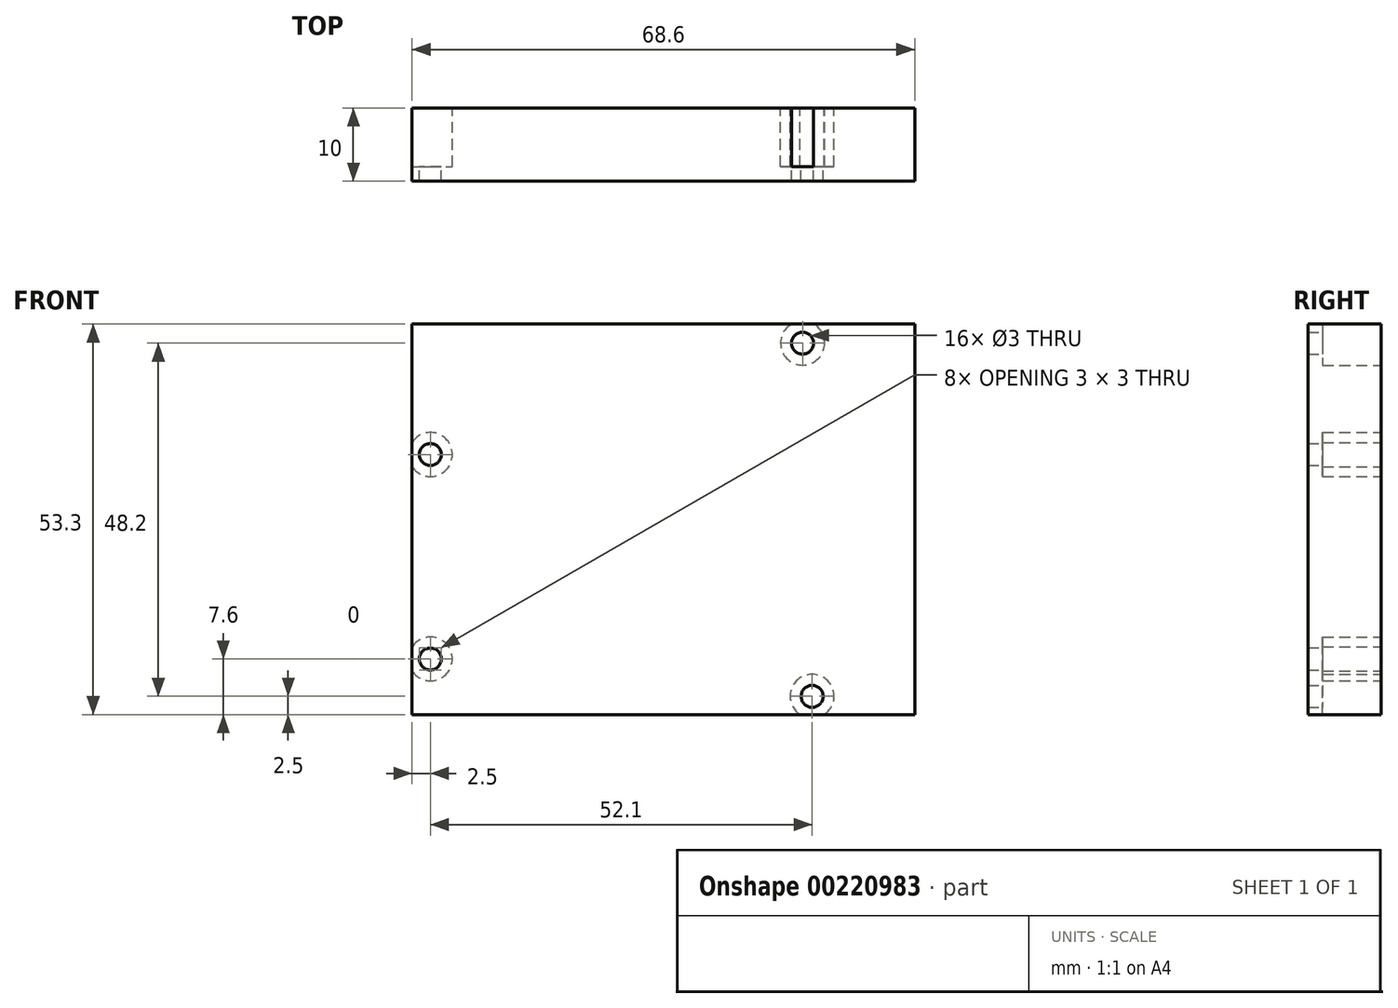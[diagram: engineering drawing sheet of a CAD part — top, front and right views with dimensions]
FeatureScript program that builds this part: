
annotation { "Feature Type Name" : "Feature", "Feature Type Description" : "" }
export const myFeature = defineFeature(function(context is Context, id is Id, definition is map)
    precondition{}
    {
        {
            var Q0;
            Q0=qCreatedBy(makeId("Front.planeOp"),FACE);
            var sketch = newSketch(context, id + "F0", { "sketchPlane" : qUnion([Q0])});
            skLineSegment(sketch, "E0.bottom", {"start": v(-34.3, 26.65) * mm, "end": v(34.3, 26.65) * mm});
            skLineSegment(sketch, "E0.top", {"start": v(-34.3, -26.65) * mm, "end": v(34.3, -26.65) * mm});
            skLineSegment(sketch, "E0.left", {"start": v(-34.3, 26.65) * mm, "end": v(-34.3, -26.65) * mm});
            skLineSegment(sketch, "E0.right", {"start": v(34.3, 26.65) * mm, "end": v(34.3, -26.65) * mm});
            skPoint(sketch, "E0.middle", {"position": v(0, 0) * mm});
            skLineSegment(sketch, "E1", {"start": v(34.3, -26.65) * mm, "end": v(34.3, -24.15) * mm});
            skLineSegment(sketch, "E2", {"start": v(34.3, -24.15) * mm, "end": v(20.3, -24.15) * mm});
            skLineSegment(sketch, "E3", {"start": v(20.3, -24.15) * mm, "end": v(19, -24.15) * mm});
            skLineSegment(sketch, "E4", {"start": v(19, -24.15) * mm, "end": v(19, 24.05) * mm});
            skLineSegment(sketch, "E5", {"start": v(19, 24.05) * mm, "end": v(-31.8, 24.05) * mm});
            skLineSegment(sketch, "E6", {"start": v(-31.8, 24.05) * mm, "end": v(-31.8, 8.85) * mm});
            skLineSegment(sketch, "E7", {"start": v(-31.8, 24.05) * mm, "end": v(-55.9, 24.05) * mm});
            skLineSegment(sketch, "E8", {"start": v(-31.8, 8.85) * mm, "end": v(-31.8, -19.05) * mm});
            skCircle(sketch, "E9", {"center": v(20.3, -24.15) * mm, "radius": 1.5 * mm});
            skCircle(sketch, "E10", {"center": v(19, 24.05) * mm, "radius": 1.5 * mm});
            skCircle(sketch, "E11", {"center": v(-31.8, 8.85) * mm, "radius": 1.5 * mm});
            skCircle(sketch, "E12", {"center": v(-31.8, -19.05) * mm, "radius": 1.5 * mm});
            skSolve(sketch);
        }
        {
            var Q0;
            Q0=qSketchRegion(id+"F0",true);
            extrude(context, id + "F1", {"entities" : qUnion([Q0]), "depth" : 10 * mm});
        }
        {
            var Q0;
            Q0=makeQuery(id+"F1.opExtrude","CAP_FACE",FACE,{"disambiguationData":[OSD([sQuery(id+"F0.wireOp",EDGE,"E0.bottom"),sQuery(id+"F0.wireOp",EDGE,"E0.top"),sQuery(id+"F0.wireOp",EDGE,"E0.left"),sQuery(id+"F0.wireOp",EDGE,"E0.right"),sQuery(id+"F0.wireOp",EDGE,"E1"),sQuery(id+"F0.wireOp",EDGE,"E9"),sQuery(id+"F0.wireOp",EDGE,"E10"),sQuery(id+"F0.wireOp",EDGE,"E11"),sQuery(id+"F0.wireOp",EDGE,"E12")])],"isStart":true});
            var sketch = newSketch(context, id + "F2", { "sketchPlane" : qUnion([Q0])});
            skCircle(sketch, "E13", {"center": v(-19, 24.05) * mm, "radius": 3 * mm});
            skCircle(sketch, "E14", {"center": v(31.8, 8.85) * mm, "radius": 3 * mm});
            skCircle(sketch, "E15", {"center": v(31.8, -19.05) * mm, "radius": 3 * mm});
            skCircle(sketch, "E16", {"center": v(-20.3, -24.15) * mm, "radius": 3 * mm});
            skSolve(sketch);
        }
        {
            var Q0;
            Q0 = qSketchRegion(id + "F2", true);
            extrude(context, id + "F3", {"entities" : qUnion([Q0]), "operationType" : NewBodyOperationType.REMOVE, "oppositeDirection" : true, "depth" : 8 * mm});
        }
    });
